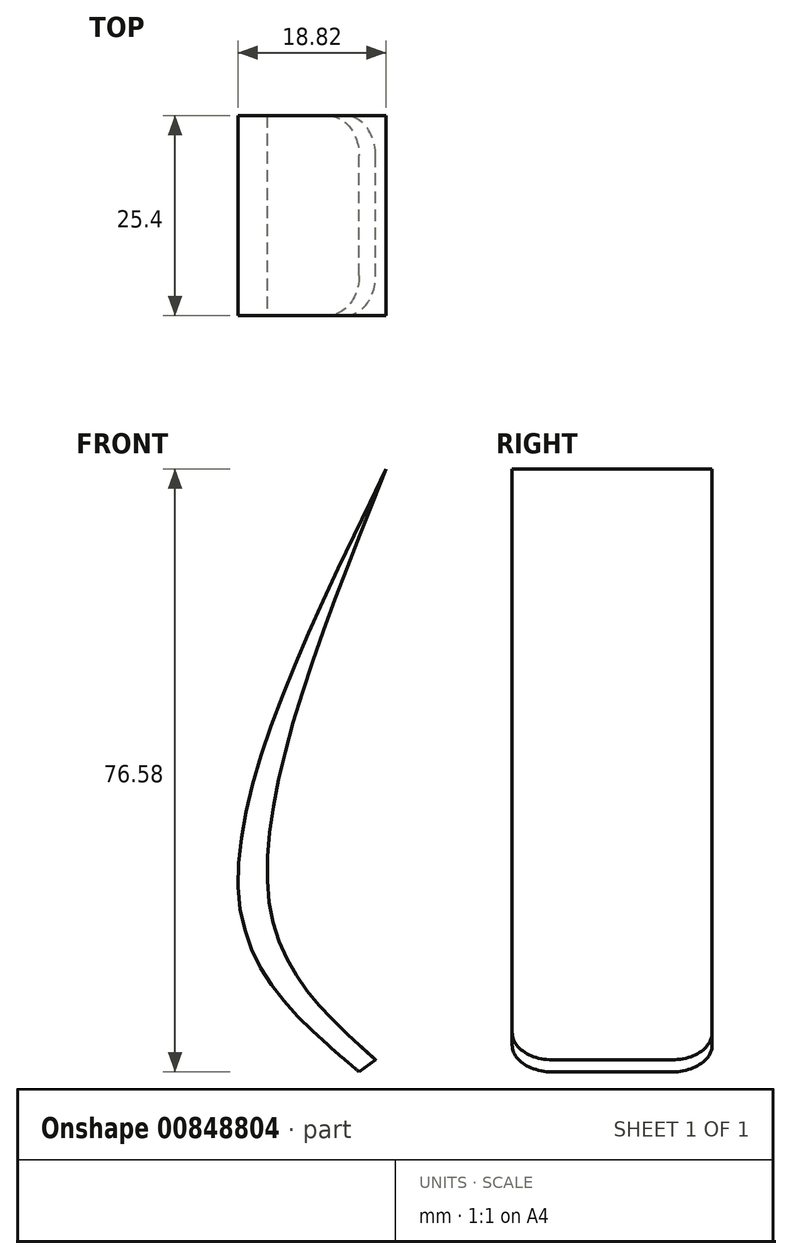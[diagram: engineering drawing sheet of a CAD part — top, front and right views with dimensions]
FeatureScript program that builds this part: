
annotation { "Feature Type Name" : "Feature", "Feature Type Description" : "" }
export const myFeature = defineFeature(function(context is Context, id is Id, definition is map)
    precondition{}
    {
        {
            var Q0;
            Q0=qCreatedBy(makeId("Front.planeOp"),FACE);
            var sketch = newSketch(context, id + "F0", { "sketchPlane" : qUnion([Q0])});
            skFitSpline(sketch, "E0", {"points": [v(-29.88, 56.05) * mm, v(-48.4, 0) * mm, v(-33.32, -20.53) * mm], "startDerivative": vector(-51.43, -105.26) * mm, "endDerivative": vector(51.68, -43.63) * mm});
            skLineSegment(sketch, "E1", {"start": v(-33.32, -20.53) * mm, "end": v(-31.22, -19) * mm});
            skFitSpline(sketch, "E2", {"points": [v(-31.22, -19) * mm, v(-44.59, 0) * mm, v(-29.88, 56.05) * mm], "startDerivative": vector(-45.82, 40.76) * mm, "endDerivative": vector(41.92, 104.55) * mm});
            skSolve(sketch);
        }
        {
            var Q0;
            Q0=makeQuery(id+"F0.imprint","IMPRINT",FACE,{"disambiguationData":[TD([[makeQuery(id+"F0.imprint","IMPRINT",EDGE,{"derivedFrom":sQuery(id+"F0.wireOp",EDGE,"E0")}),1.0]])]});
            extrude(context, id + "F1", {"entities" : qUnion([Q0]), "depth" : 25.4 * mm, "offsetDistance" : 25.4 * mm});
        }
        {
            var Q0;
            Q0=makeQuery(id+"F1.opExtrude","CAP_EDGE",EDGE,{"disambiguationData":[OSD([sQuery(id+"F0.wireOp",EDGE,"E1")])],"isStart":true});
            var Q1;
            Q1=makeQuery(id+"F1.opExtrude","CAP_EDGE",EDGE,{"disambiguationData":[OSD([sQuery(id+"F0.wireOp",EDGE,"E1")])],"isStart":false});
            fillet(context, id + "F2", {"entities" : qUnion([Q0, Q1]), "radius" : 5.08 * mm, "tangentPropagation" : true, "allowEdgeOverflow" : false});
        }
        {
            var Q0;
            Q0=makeQuery(id+"F1.opExtrude","CAP_FACE",FACE,{"disambiguationData":[OSD([sQuery(id+"F0.wireOp",EDGE,"E0"),sQuery(id+"F0.wireOp",EDGE,"E1"),sQuery(id+"F0.wireOp",EDGE,"E2")])],"isStart":false});
            var sketch = newSketch(context, id + "F3", { "sketchPlane" : qUnion([Q0])});
            skLineSegment(sketch, "E3", {"start": v(-35.06, -15.51) * mm, "end": v(-37.28, -17.13) * mm});
            skLineSegment(sketch, "E4", {"start": v(-39.05, -15.51) * mm, "end": v(-37.28, -13.3) * mm});
            skLineSegment(sketch, "E5", {"start": v(-37.28, -13.3) * mm, "end": v(-35.06, -15.51) * mm});
            skSolve(sketch);
        }
        {
            var Q0;
            {var subQ0=sQuery(id+"F3.wireOp",EDGE,"E3");Q0=makeQuery(id+"F3.imprint","IMPRINT",FACE,{"disambiguationData":[TD([[makeQuery(id+"F3.imprint","IMPRINT",EDGE,{"derivedFrom":subQ0}),1.0]])]});}
            extrude(context, id + "F4", {"entities" : qUnion([Q0]), "operationType" : NewBodyOperationType.ADD, "depth" : -19.05 * mm, "offsetDistance" : 25.4 * mm});
        }
    });
